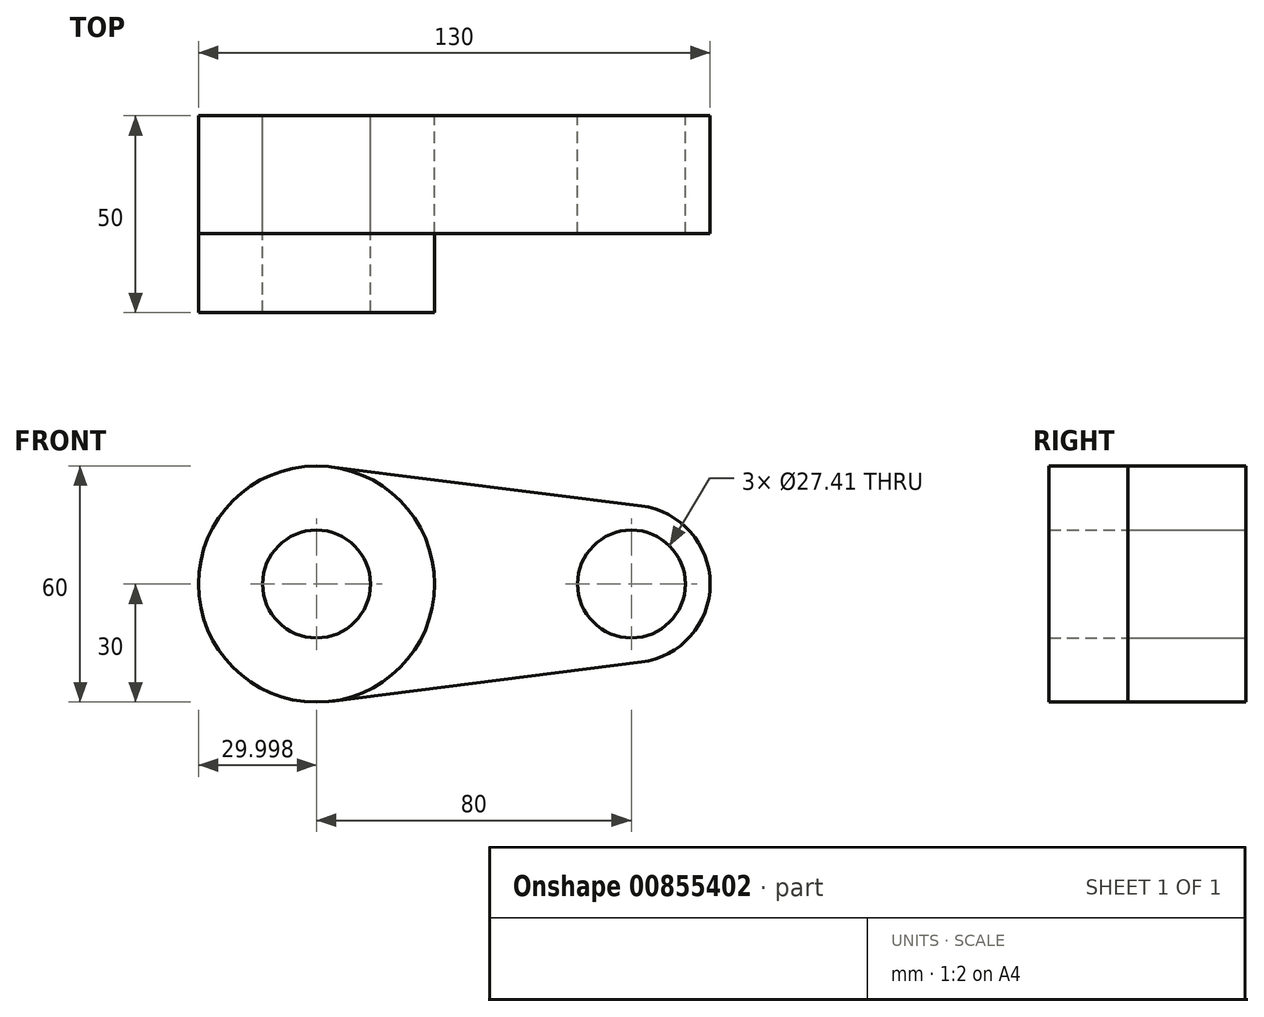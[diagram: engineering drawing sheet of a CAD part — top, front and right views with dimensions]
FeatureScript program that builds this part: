
annotation { "Feature Type Name" : "Feature", "Feature Type Description" : "" }
export const myFeature = defineFeature(function(context is Context, id is Id, definition is map)
    precondition{}
    {
        {
            var Q0;
            Q0=qCreatedBy(makeId("Front.planeOp"),FACE);
            var sketch = newSketch(context, id + "F0", { "sketchPlane" : qUnion([Q0])});
            skCircle(sketch, "E0", {"center": v(-29.27, 0) * mm, "radius": 30 * mm});
            skCircle(sketch, "E1", {"center": v(50.73, 0) * mm, "radius": 20 * mm});
            skLineSegment(sketch, "E2", {"start": v(-25.52, 29.76) * mm, "end": v(53.23, 19.84) * mm});
            skLineSegment(sketch, "E3", {"start": v(-25.52, -29.76) * mm, "end": v(53.23, -19.84) * mm});
            skCircle(sketch, "E4", {"center": v(-29.27, 0) * mm, "radius": 13.7 * mm});
            skCircle(sketch, "E5", {"center": v(50.73, 0) * mm, "radius": 13.7 * mm});
            skSolve(sketch);
        }
        {
            var Q0;
            Q0=makeQuery(id+"F0.imprint","IMPRINT",FACE,{"disambiguationData":[TD([[makeQuery(id+"F0.imprint","IMPRINT",EDGE,{"derivedFrom":sQuery(id+"F0.wireOp",EDGE,"E4")}),-1.0]])]});
            var Q1;
            Q1=makeQuery(id+"F0.imprint","IMPRINT",FACE,{"disambiguationData":[TD([[makeQuery(id+"F0.imprint","IMPRINT",EDGE,{"derivedFrom":sQuery(id+"F0.wireOp",EDGE,"E5")}),-1.0]])]});
            var Q2;
            {var subQ0=sQuery(id+"F0.wireOp",EDGE,"E2");Q2=makeQuery(id+"F0.imprint","IMPRINT",FACE,{"disambiguationData":[TD([[makeQuery(id+"F0.imprint","IMPRINT",EDGE,{"derivedFrom":subQ0}),-1.0]])]});}
            extrude(context, id + "F1", {"entities" : qUnion([Q0, Q1, Q2]), "depth" : 30 * mm, "offsetDistance" : 25 * mm});
        }
        {
            var Q0;
            Q0=makeQuery(id+"F0.imprint","IMPRINT",FACE,{"disambiguationData":[TD([[makeQuery(id+"F0.imprint","IMPRINT",EDGE,{"derivedFrom":sQuery(id+"F0.wireOp",EDGE,"E4")}),-1.0]])]});
            extrude(context, id + "F2", {"entities" : qUnion([Q0]), "depth" : 50 * mm, "offsetDistance" : 25 * mm});
        }
    });
